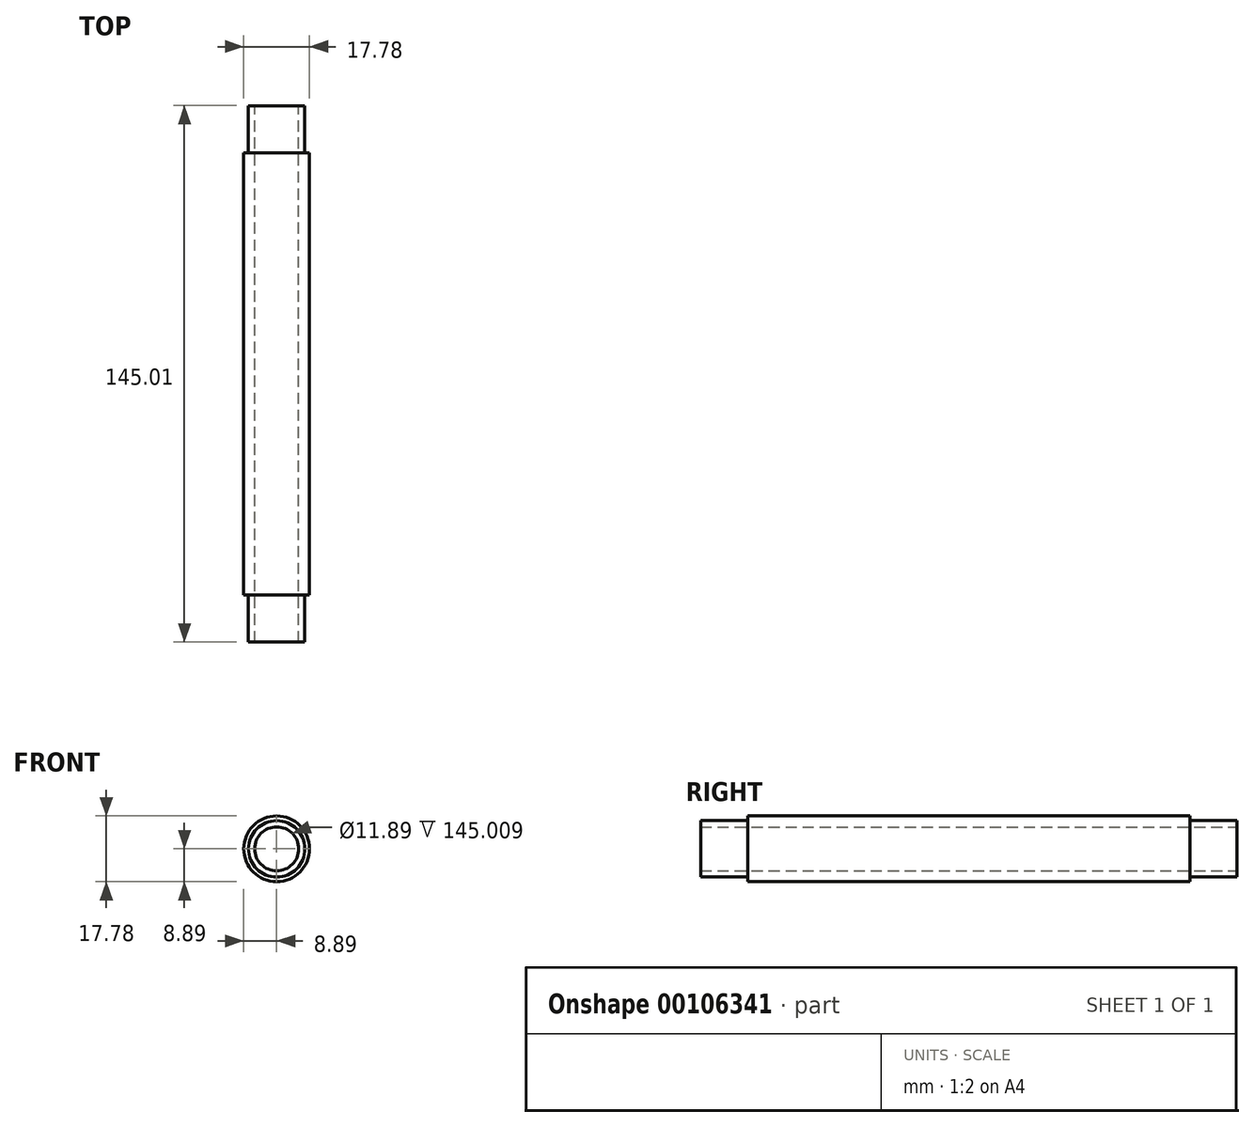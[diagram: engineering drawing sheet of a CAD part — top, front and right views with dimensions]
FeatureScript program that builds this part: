
annotation { "Feature Type Name" : "Feature", "Feature Type Description" : "" }
export const myFeature = defineFeature(function(context is Context, id is Id, definition is map)
    precondition{}
    {
        {
            var Q0;
            Q0=qCreatedBy(makeId("Top.planeOp"),FACE);
            var sketch = newSketch(context, id + "F0", { "sketchPlane" : qUnion([Q0])});
            skLineSegment(sketch, "E0", {"start": v(0, 0) * mm, "end": v(0, 145) * mm});
            skSolve(sketch);
        }
        {
            var Q0;
            Q0=qCreatedBy(makeId("Front.planeOp"),FACE);
            var sketch = newSketch(context, id + "F1", { "sketchPlane" : qUnion([Q0])});
            skCircle(sketch, "E1", {"center": v(0, 0) * mm, "radius": 8.9 * mm});
            skCircle(sketch, "E2", {"center": v(0, 0) * mm, "radius": 5.94 * mm});
            skSolve(sketch);
        }
        {
            var Q0;
            Q0=makeQuery(id+"F1.imprint","IMPRINT",FACE,{"disambiguationData":[TD([[makeQuery(id+"F1.imprint","IMPRINT",EDGE,{"derivedFrom":sQuery(id+"F1.wireOp",EDGE,"E1")}),1.0]])]});
            var Q1;
            Q1=sQuery(id+"F0.wireOp",EDGE,"E0");
            sweep(context, id + "F2", {"profiles" : qUnion([Q0]), "path" : qUnion([Q1])});
        }
        {
            var Q0;
            Q0=makeQuery(id+"F2.opSweep","CAP_FACE",FACE,{"disambiguationData":[OSD([sQuery(id+"F0.wireOp",VERTEX,"E0.start"),sQuery(id+"F1.wireOp",EDGE,"E1"),sQuery(id+"F1.wireOp",EDGE,"E2")])],"isStart":true});
            var sketch = newSketch(context, id + "F3", { "sketchPlane" : qUnion([Q0])});
            skCircle(sketch, "E3", {"center": v(0, 0) * mm, "radius": 7.62 * mm});
            skSolve(sketch);
        }
        {
            var Q0;
            Q0=makeQuery(id+"F3.imprint","IMPRINT",FACE,{"disambiguationData":[TD([[makeQuery(id+"F3.imprint","IMPRINT",EDGE,{"derivedFrom":sQuery(id+"F3.wireOp",EDGE,"E3")}),-1.0]])]});
            extrude(context, id + "F4", {"entities" : qUnion([Q0]), "operationType" : NewBodyOperationType.REMOVE, "oppositeDirection" : true, "depth" : 12.7 * mm});
        }
        {
            var Q0;
            Q0=makeQuery(id+"F2.opSweep","CAP_FACE",FACE,{"disambiguationData":[OSD([sQuery(id+"F0.wireOp",VERTEX,"E0.end"),sQuery(id+"F1.wireOp",EDGE,"E1"),sQuery(id+"F1.wireOp",EDGE,"E2")])],"isStart":false});
            var sketch = newSketch(context, id + "F5", { "sketchPlane" : qUnion([Q0])});
            skCircle(sketch, "E4", {"center": v(0, 0) * mm, "radius": 7.62 * mm});
            skSolve(sketch);
        }
        {
            var Q0;
            Q0=makeQuery(id+"F5.imprint","IMPRINT",FACE,{"disambiguationData":[TD([[makeQuery(id+"F5.imprint","IMPRINT",EDGE,{"derivedFrom":sQuery(id+"F5.wireOp",EDGE,"E4")}),-1.0]])]});
            extrude(context, id + "F6", {"entities" : qUnion([Q0]), "operationType" : NewBodyOperationType.REMOVE, "oppositeDirection" : true, "depth" : 12.7 * mm});
        }
    });
